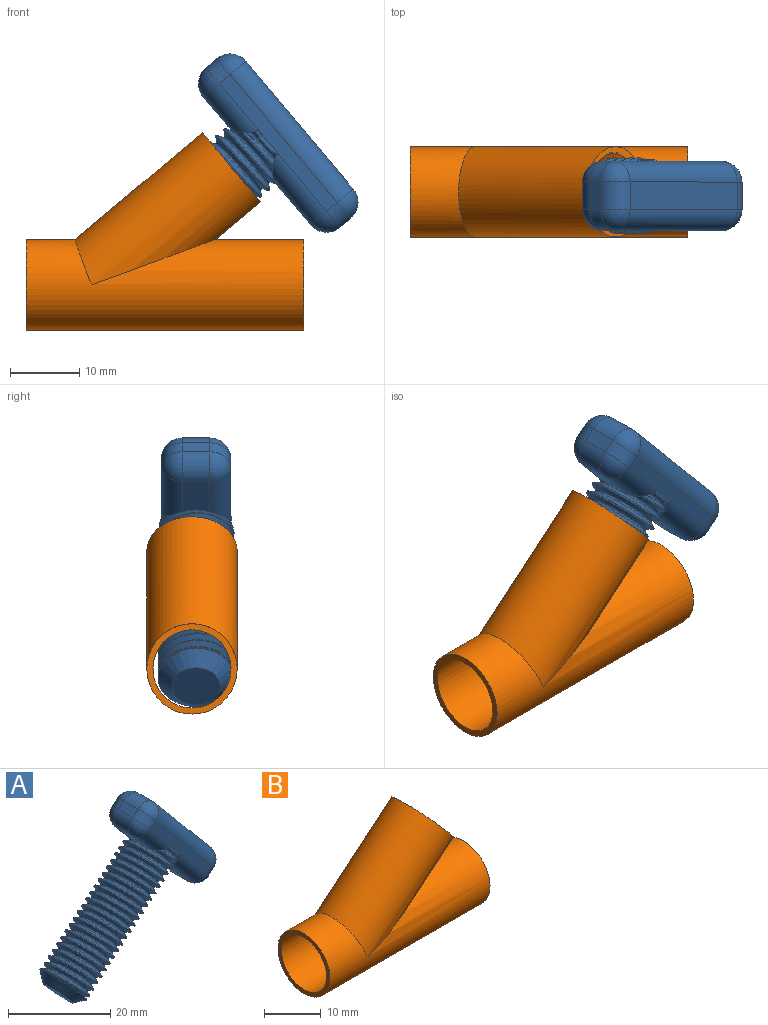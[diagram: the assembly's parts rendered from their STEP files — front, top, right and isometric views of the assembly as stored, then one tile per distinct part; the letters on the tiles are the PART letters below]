
ASSEMBLY  parts=2 mates=1
PART A: 54 faces, bbox 42.8x12.7x39 mm
  f0: cylinder r=5.47mm len=0.18mm, axis (0.77,0,0.64), area 0mm2, adj f16,f38,f41,f50
  f1: cylinder r=5.47mm len=0.26mm, axis (0.77,0,0.64), area 0mm2, adj f16,f33,f44,f50
  f2: cylinder r=5.47mm len=0.78mm, axis (0.77,0,0.64), area 0.1mm2, adj f15,f29,f44,f50
  f3: cylinder r=5.47mm len=1.07mm, axis (0.77,0,0.64), area 0.2mm2, adj f15,f34,f44,f50
  f4: cylinder r=5.47mm len=5.45mm, axis (0.77,0,0.64), area 1.3mm2, adj f33,f38,f44,f50
  f5: cylinder r=5.47mm len=7.01mm, axis (0.77,0,0.64), area 1.8mm2, adj f29,f34,f44,f50
  f6: cylinder r=5.47mm len=30.84mm, axis (0.77,0,0.64), area 386.9mm2, adj f9,f38,f39,f44,f50
  f7: plane 6.95x5.32mm, normal (-0.77,0,-0.64), area 37.9mm2, adj f39
  f8: plane 4.45x4mm, normal (-0.77,0,-0.64), area 22.2mm2, adj f29,f31,f33,f52
  f9: plane 6.13x5.14mm, normal (-0.77,0,-0.64), area 31mm2, adj f6,f34,f36,f38,f47
  f10: plane 4x1.53mm, normal (-0.64,0,0.77), area 8mm2, adj f17,f18,f24,f31
  f11: plane 19.67x16.96mm, normal (0,-1,0), area 48mm2, adj f16,f17,f19,f21,f33,f38,f40,f43
  f12: plane 4x1.53mm, normal (0.64,0,-0.77), area 8mm2, adj f19,f20,f25,f36
  f13: plane 19.67x16.96mm, normal (0,1,0), area 48mm2, adj f18,f20,f28,f29,f34,f43
  f14: plane 18.39x15.43mm, normal (0.77,0,0.64), area 96mm2, adj f21,f24,f25,f28
  f15: cylinder r=3mm len=3.2mm, axis (-0.64,0,0.77), area 1.6mm2, adj f2,f3,f44,f50
  f16: cylinder r=3mm len=3.79mm, axis (0.64,0,-0.77), area 2.1mm2, adj f0,f1,f11,f41,f44,f50
  f17: cylinder r=3mm len=3.58mm, axis (0.77,0,0.64), area 9.4mm2, adj f10,f11,f22,f32
  f18: cylinder r=3mm len=3.58mm, axis (-0.77,0,-0.64), area 9.4mm2, adj f10,f13,f26,f30
  f19: cylinder r=3mm len=3.58mm, axis (-0.77,0,-0.64), area 9.4mm2, adj f11,f12,f23,f37
  f20: cylinder r=3mm len=3.58mm, axis (0.77,0,0.64), area 9.4mm2, adj f12,f13,f27,f35
  f21: cylinder r=3mm len=20.31mm, axis (-0.64,0,0.77), area 113.1mm2, adj f11,f14,f22,f23
  f22: sphere r=3mm, area 14.1mm2, adj f17,f21,f24
  f23: sphere r=3mm, area 14.1mm2, adj f19,f21,f25
  f24: cylinder r=3mm len=4.23mm, axis (0,1,0), area 18.8mm2, adj f10,f14,f22,f26
  f25: cylinder r=3mm len=4.23mm, axis (0,-1,0), area 18.8mm2, adj f12,f14,f23,f27
  f26: sphere r=3mm, area 14.1mm2, adj f18,f24,f28
  f27: sphere r=3mm, area 14.1mm2, adj f20,f25,f28
  f28: cylinder r=3mm len=20.31mm, axis (0.64,0,-0.77), area 113.1mm2, adj f13,f14,f26,f27
  f29: cylinder r=3mm len=8.57mm, axis (-0.64,0,0.77), area 34.5mm2, adj f2,f5,f8,f13,f30,f45,f46,f52
  f30: sphere r=3mm, area 14.1mm2, adj f18,f29,f31
  f31: cylinder r=3mm len=4.23mm, axis (0,-1,0), area 18.8mm2, adj f8,f10,f30,f32
  f32: sphere r=3mm, area 14.1mm2, adj f17,f31,f33
  f33: cylinder r=3mm len=8.57mm, axis (0.64,0,-0.77), area 34.3mm2, adj f1,f4,f8,f11,f32,f45,f46,f52
  f34: cylinder r=3mm len=10.26mm, axis (-0.64,0,0.77), area 44.7mm2, adj f3,f5,f9,f13,f35,f47,f48,f49
  f35: sphere r=3mm, area 14.1mm2, adj f20,f34,f36
  f36: cylinder r=3mm len=4.23mm, axis (0,1,0), area 18.8mm2, adj f9,f12,f35,f37
  f37: sphere r=3mm, area 14.1mm2, adj f19,f36,f38
  f38: cylinder r=3mm len=10.26mm, axis (0.64,0,-0.77), area 44.8mm2, adj f0,f4,f6,f9,f11,f37,f42,f48
  f39: cone r=5.47mm half-angle=45deg, axis (0.77,0,0.64), area 79.5mm2, adj f6,f7,f53
  f40: plane 1.67x1.4mm, normal (-0.77,0,-0.64), area 0.2mm2, adj f11,f41,f42
  f41: bspline ~6.32x6.05mm, area 0.2mm2, adj f0,f16,f40,f42
  f42: cylinder r=5.47mm len=1.34mm, axis (-0.77,0,-0.64), area 0.1mm2, adj f38,f40,f41
  f43: plane 10.07x8.45mm, normal (-0.77,0,-0.64), area 12.4mm2, adj f11,f13,f44,f45,f48,f50,f51
  f44: bspline ~31.94x30.24mm, area 672mm2, adj f1,f2,f3,f4,f5,f6,f15,f16
  f45: cylinder r=5.47mm len=10mm, axis (-0.77,0,-0.64), area 7mm2, adj f29,f33,f43,f44
  f46: cylinder r=5.47mm len=9.79mm, axis (-0.77,0,-0.64), area 14.2mm2, adj f29,f33,f44,f50
  f47: cylinder r=5.47mm len=2.88mm, axis (-0.77,0,-0.64), area 0.1mm2, adj f9,f34,f50
  f48: cylinder r=5.47mm len=9.99mm, axis (-0.77,0,-0.64), area 14.9mm2, adj f34,f38,f43,f44,f50
  f49: cylinder r=5.47mm len=9.18mm, axis (-0.77,0,-0.64), area 11.4mm2, adj f34,f38,f44,f50
  f50: bspline ~33.08x29.28mm, area 672.7mm2, adj f0,f1,f2,f3,f4,f5,f6,f15
  f51: bspline ~32.23x29.24mm, area 277.3mm2, adj f43,f44,f50,f53
  f52: cylinder r=5.47mm len=7.96mm, axis (-0.77,0,-0.64), area 4.9mm2, adj f8,f29,f33,f50
  f53: plane 10.84x8.45mm, normal (0.77,0,0.64), area 15.2mm2, adj f39,f44,f50,f51
PART B: 46 faces, bbox 40.4x13.7x28.9 mm
  f0: bspline ~13.13x6.94mm, area 14.8mm2, adj f16,f31,f41
  f1: bspline ~13.13x6.94mm, area 17.2mm2, adj f17,f30,f41
  f2: bspline ~13.13x6.94mm, area 18.7mm2, adj f18,f29,f41
  f3: bspline ~13.13x8.39mm, area 20mm2, adj f19,f28,f41
  f4: bspline ~13.13x9.28mm, area 21.4mm2, adj f20,f27,f41
  f5: bspline ~13.13x9.28mm, area 22.8mm2, adj f21,f26,f41
  f6: bspline ~13.13x9.28mm, area 24.4mm2, adj f22,f25,f41
  f7: bspline ~13.13x9.28mm, area 26.6mm2, adj f23,f40,f41
  f8: bspline ~13.13x6.94mm, area 0mm2, adj f16,f41
  f9: bspline ~13.13x6.94mm, area 16mm2, adj f17,f31,f41
  f10: bspline ~13.13x6.94mm, area 17.9mm2, adj f18,f30,f41
  f11: bspline ~13.13x6.94mm, area 19.4mm2, adj f19,f29,f41
  f12: bspline ~13.13x9.28mm, area 20.7mm2, adj f20,f28,f41
  f13: bspline ~13.13x9.28mm, area 22.1mm2, adj f21,f27,f41
  f14: bspline ~13.13x9.28mm, area 23.6mm2, adj f22,f26,f41
  f15: bspline ~13.13x9.28mm, area 25.4mm2, adj f23,f25,f41
  f16: bspline ~13.29x7.08mm, area 4.4mm2, adj f0,f8,f41
  f17: bspline ~13.29x7.08mm, area 4.6mm2, adj f1,f9,f41
  f18: bspline ~13.29x7.08mm, area 4.9mm2, adj f2,f10,f41
  f19: bspline ~13.29x8.55mm, area 5.1mm2, adj f3,f11,f41
  f20: bspline ~13.29x9.43mm, area 5.4mm2, adj f4,f12,f41
  f21: bspline ~13.29x9.43mm, area 5.7mm2, adj f5,f13,f41
  f22: bspline ~13.29x9.43mm, area 6mm2, adj f6,f14,f41
  f23: bspline ~13.29x9.43mm, area 6.4mm2, adj f7,f15,f41
  f24: bspline ~13.29x9.43mm, area 7mm2, adj f37,f38,f41
  f25: cylinder r=4.88mm len=9.75mm, axis (-0.77,0,-0.64), area 9.3mm2, adj f6,f15,f41
  f26: cylinder r=4.88mm len=9.75mm, axis (-0.77,0,-0.64), area 8.5mm2, adj f5,f14,f41
  f27: cylinder r=4.88mm len=9.75mm, axis (-0.77,0,-0.64), area 7.9mm2, adj f4,f13,f41
  f28: cylinder r=4.88mm len=9.75mm, axis (-0.77,0,-0.64), area 7.3mm2, adj f3,f12,f41
  f29: cylinder r=4.88mm len=9.75mm, axis (-0.77,0,-0.64), area 6.7mm2, adj f2,f11,f41
  f30: cylinder r=4.88mm len=9.75mm, axis (-0.77,0,-0.64), area 6mm2, adj f1,f10,f41
  f31: cylinder r=4.88mm len=9.5mm, axis (-0.77,0,-0.64), area 4.7mm2, adj f0,f9,f41
  f32: plane 13.45x10.41mm, normal (0.77,0,0.64), area 46.4mm2, adj f36,f37,f38,f39,f40
  f33: cylinder r=6.5mm len=40mm, axis (-1,0,0), area 1370.8mm2, adj f34,f35,f36
  f34: plane 13x13mm, normal (1,0,0), area 33.3mm2, adj f33,f41
  f35: plane 13x13mm, normal (-1,0,0), area 33.3mm2, adj f33,f41
  f36: cylinder r=6.5mm len=28.43mm, axis (-0.77,0,-0.64), area 813.3mm2, adj f32,f33
  f37: bspline ~15.73x15.73mm, area 253.5mm2, adj f24,f32,f39,f40,f41
  f38: bspline ~16.99x16.12mm, area 264mm2, adj f24,f32,f39,f40,f41
  f39: bspline ~16.1x15.12mm, area 57.8mm2, adj f32,f37,f38,f41
  f40: cylinder r=4.88mm len=16.52mm, axis (-0.77,0,-0.64), area 105.4mm2, adj f7,f32,f37,f38,f41
  f41: cylinder r=5.62mm len=40mm, axis (1,0,0), area 1252.8mm2, adj f0,f1,f2,f3,f4,f5,f6,f7
  f42: bspline ~6.65x6.43mm, area 0.6mm2, adj f41,f43,f44,f45
  f43: bspline ~4.2x3.95mm, area 0mm2, adj f41,f42,f45
  f44: bspline ~6.57x6.29mm, area 1.2mm2, adj f41,f42,f45
  f45: plane 3.69x3.11mm, normal (0.77,0,0.64), area 0.9mm2, adj f41,f42,f43,f44
PLACE A t=(-3.71,1.28,2.31)mm
PLACE B t=(-6.72,1.86,0.55)mm fixed
MATE slider B.f32 <-> A.f0  axis (0.77,0,0.64) through (3.22,1.28,17.04)mm
